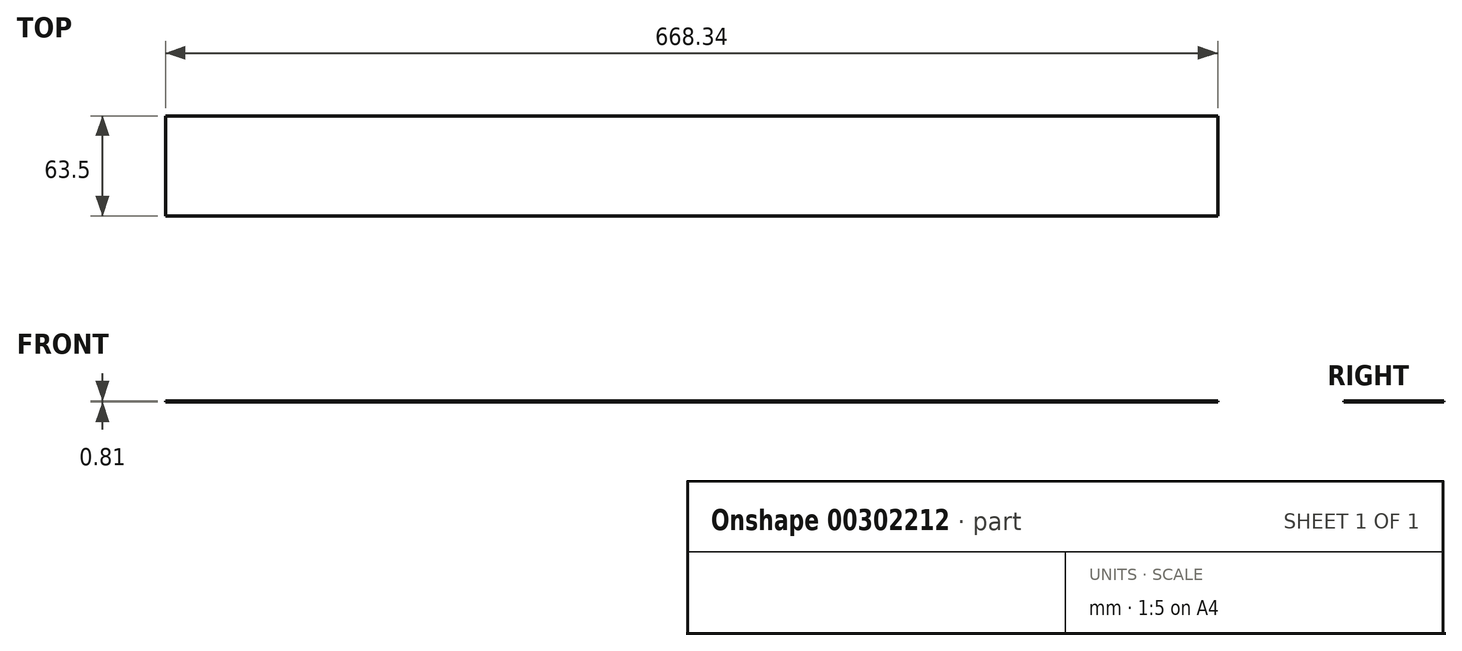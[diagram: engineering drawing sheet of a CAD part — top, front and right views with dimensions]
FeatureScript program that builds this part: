
annotation { "Feature Type Name" : "Feature", "Feature Type Description" : "" }
export const myFeature = defineFeature(function(context is Context, id is Id, definition is map)
    precondition{}
    {
        {
            var Q0;
            Q0=qCreatedBy(makeId("Top.planeOp"),FACE);
            var sketch = newSketch(context, id + "F0", { "sketchPlane" : qUnion([Q0])});
            skLineSegment(sketch, "E0.bottom", {"start": v(0, 0) * mm, "end": v(668.34, 0) * mm});
            skLineSegment(sketch, "E0.top", {"start": v(0, 63.5) * mm, "end": v(668.34, 63.5) * mm});
            skLineSegment(sketch, "E0.left", {"start": v(0, 0) * mm, "end": v(0, 63.5) * mm});
            skLineSegment(sketch, "E0.right", {"start": v(668.34, 0) * mm, "end": v(668.34, 63.5) * mm});
            skLineSegment(sketch, "E1.bottom", {"start": v(655.64, 63.5) * mm, "end": v(623.89, 63.5) * mm});
            skLineSegment(sketch, "E1.top", {"start": v(655.64, 133.35) * mm, "end": v(623.89, 133.35) * mm});
            skLineSegment(sketch, "E1.left", {"start": v(655.64, 63.5) * mm, "end": v(655.64, 133.35) * mm});
            skLineSegment(sketch, "E1.right", {"start": v(623.89, 63.5) * mm, "end": v(623.89, 133.35) * mm});
            skLineSegment(sketch, "E2.bottom", {"start": v(563.56, 63.5) * mm, "end": v(542.48, 63.5) * mm});
            skLineSegment(sketch, "E2.top", {"start": v(563.56, 133.35) * mm, "end": v(542.48, 133.35) * mm});
            skLineSegment(sketch, "E2.left", {"start": v(563.56, 63.5) * mm, "end": v(563.56, 133.35) * mm});
            skLineSegment(sketch, "E2.right", {"start": v(542.48, 63.5) * mm, "end": v(542.48, 133.35) * mm});
            skLineSegment(sketch, "E3.bottom", {"start": v(482.16, 63.5) * mm, "end": v(85.92, 63.5) * mm});
            skLineSegment(sketch, "E3.top", {"start": v(482.16, 133.35) * mm, "end": v(85.92, 133.35) * mm});
            skLineSegment(sketch, "E3.left", {"start": v(482.16, 63.5) * mm, "end": v(482.16, 133.35) * mm});
            skLineSegment(sketch, "E3.right", {"start": v(85.92, 63.5) * mm, "end": v(85.92, 133.35) * mm});
            skSolve(sketch);
        }
        {
            var Q0;
            Q0=makeQuery(id+"F0.imprint","IMPRINT",FACE,{"disambiguationData":[TD([[makeQuery(id+"F0.imprint","IMPRINT",EDGE,{"derivedFrom":sQuery(id+"F0.wireOp",EDGE,"E0.bottom")}),1.0]])]});
            var Q1;
            Q1=makeQuery(id+"F0.imprint","IMPRINT",FACE,{"disambiguationData":[TD([[makeQuery(id+"F0.imprint","IMPRINT",EDGE,{"derivedFrom":sQuery(id+"F0.wireOp",EDGE,"E3.bottom")}),-1.0]])]});
            var Q2;
            Q2=makeQuery(id+"F0.imprint","IMPRINT",FACE,{"disambiguationData":[TD([[makeQuery(id+"F0.imprint","IMPRINT",EDGE,{"derivedFrom":sQuery(id+"F0.wireOp",EDGE,"E2.bottom")}),-1.0]])]});
            var Q3;
            Q3=makeQuery(id+"F0.imprint","IMPRINT",FACE,{"disambiguationData":[TD([[makeQuery(id+"F0.imprint","IMPRINT",EDGE,{"derivedFrom":sQuery(id+"F0.wireOp",EDGE,"E1.bottom")}),-1.0]])]});
            extrude(context, id + "F1", {"entities" : qUnion([Q0, Q1, Q2, Q3]), "depth" : 0.81 * mm});
        }
    });
